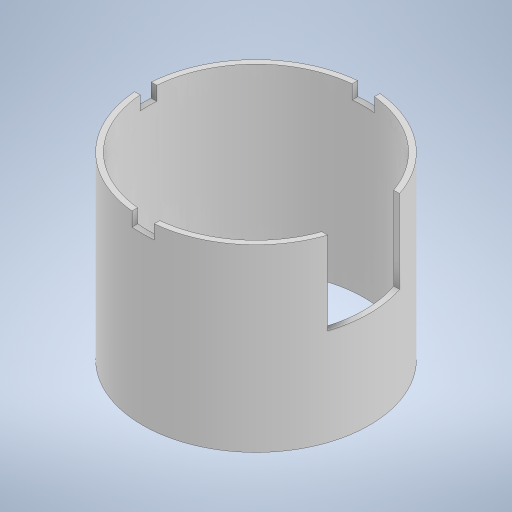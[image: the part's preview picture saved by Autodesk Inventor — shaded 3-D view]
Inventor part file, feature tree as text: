
AUTODESK INVENTOR PART (.ipt)
format: ipt  version: 2024 (Build 280153000, 153)  size: 245,760 bytes
history: native  units: in
note: dims shown in document units (in); Inventor stores cm internally (conversion verified against a paired STEP export)
features: extrude x5, sketch x5
ambient origin geometry x8: Origin, YZ Plane, XZ Plane, XY Plane, X Axis, Y Axis, Z Axis, Center Point
bodies: Solid1 (feature_tree)
feature tree (10):
  extrude  "Extrusion1"  Depth=3.0709in
  extrude  "Extrusion2"  Depth=0.315in
  extrude  "Extrusion3"  Depth=0.1969in TaperAngle=0.0deg
  extrude  "Extrusion4"  TaperAngle=90.0deg  [1 undecoded]
  extrude  "Extrusion5"  Depth=1.0236in TaperAngle=0.0deg
  sketch  "Sketch1"  dims[d0=3.2283in d1=3.0709in]
  sketch  "Sketch2"  dims[d2=2.5591in d3=0.0in d4=0.315in]
  sketch  "Sketch3"  dims[d5=3.2283in d6=0.1969in d7=0.0in]
  sketch  "Sketch4"  dims[d8=0.2362in d9=90.0deg]
  sketch  "Sketch5"  dims[d10=3.2283in d11=0.1969in d12=0.0in d13=0.5118in d14=1.0236in d15=3.2283in d16=1.1811in d17=0.0in d18=0.315in d19=3.2283in d20=0.0in]
note: 1 required parameter value undecoded (feature->parameter linkage not recoverable at this tier; creation-order binding heuristic only, values carry confidence <= 0.55)
